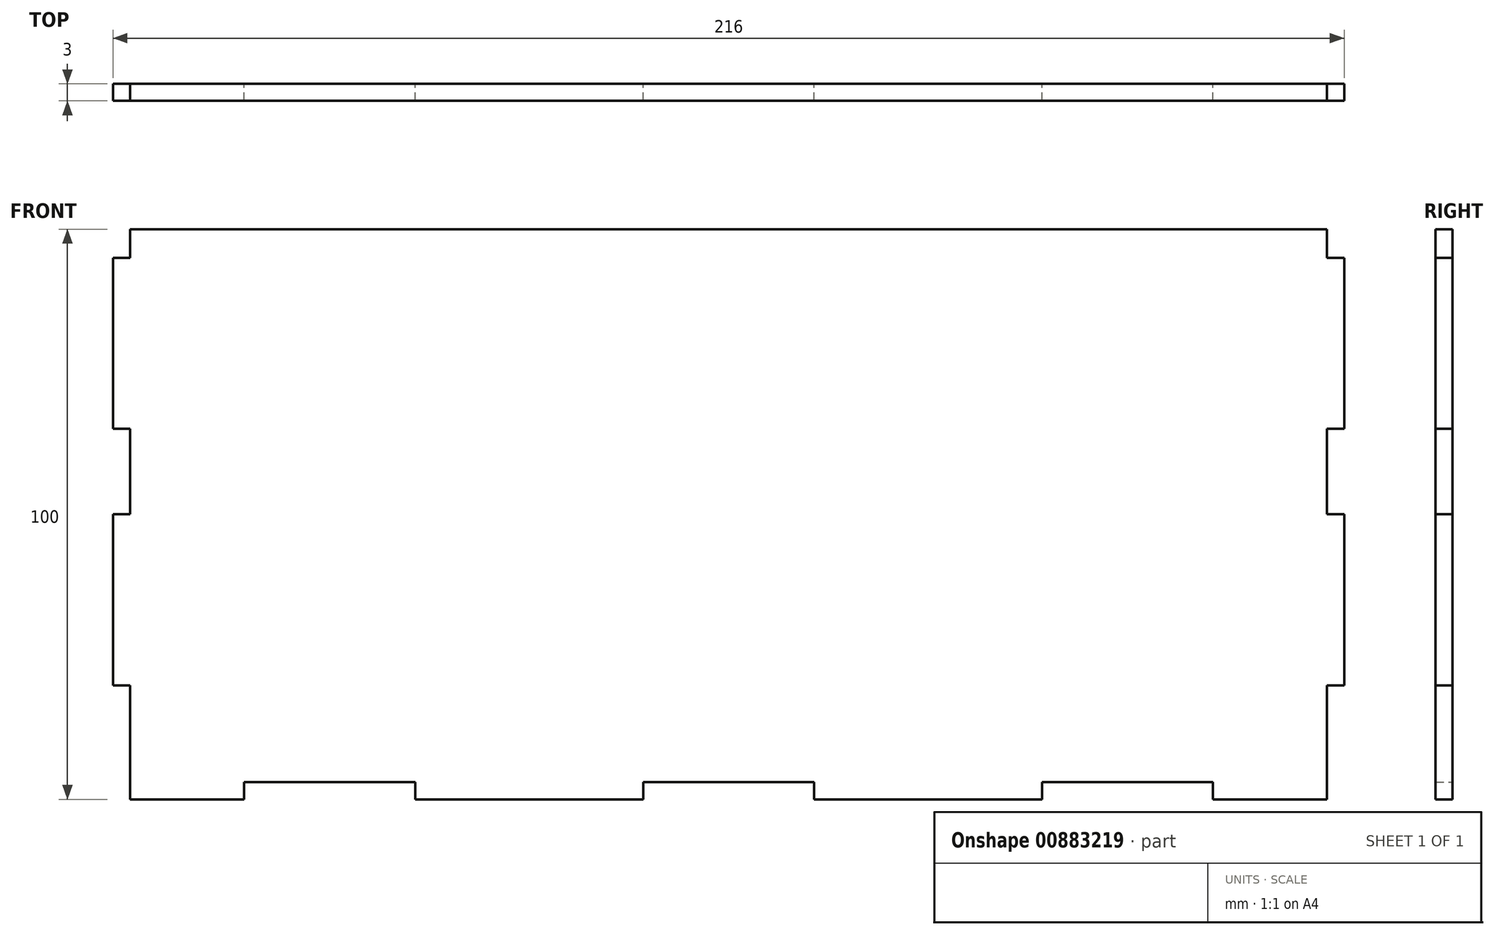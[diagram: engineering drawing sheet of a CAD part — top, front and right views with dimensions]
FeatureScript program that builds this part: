
annotation { "Feature Type Name" : "Feature", "Feature Type Description" : "" }
export const myFeature = defineFeature(function(context is Context, id is Id, definition is map)
    precondition{}
    {
        {
            var Q0;
            Q0=qCreatedBy(makeId("Front.planeOp"),FACE);
            var sketch = newSketch(context, id + "F0", { "sketchPlane" : qUnion([Q0])});
            skLineSegment(sketch, "E0.bottom", {"start": v(105, 50) * mm, "end": v(-105, 50) * mm});
            skLineSegment(sketch, "E0.top", {"start": v(105, -50) * mm, "end": v(-105, -50) * mm});
            skLineSegment(sketch, "E0.left", {"start": v(105, 50) * mm, "end": v(105, -50) * mm});
            skLineSegment(sketch, "E0.right", {"start": v(-105, 50) * mm, "end": v(-105, -50) * mm});
            skPoint(sketch, "E0.middle", {"position": v(0, 0) * mm});
            skLineSegment(sketch, "E1", {"start": v(55, -50) * mm, "end": v(55, -47) * mm});
            skLineSegment(sketch, "E2", {"start": v(55, -47) * mm, "end": v(85, -47) * mm});
            skLineSegment(sketch, "E3", {"start": v(85, -47) * mm, "end": v(85, -50) * mm});
            skLineSegment(sketch, "E4", {"start": v(105, -30) * mm, "end": v(108, -30) * mm});
            skLineSegment(sketch, "E5", {"start": v(108, -30) * mm, "end": v(108, 0) * mm});
            skLineSegment(sketch, "E6", {"start": v(108, 0) * mm, "end": v(105, 0) * mm});
            skLineSegment(sketch, "E7.MirrorCS", {"start": v(-105, -30) * mm, "end": v(-108, -30) * mm});
            skLineSegment(sketch, "E8.MirrorCS", {"start": v(-108, -30) * mm, "end": v(-108, 0) * mm});
            skLineSegment(sketch, "E9.MirrorCS", {"start": v(-108, 0) * mm, "end": v(-105, 0) * mm});
            skLineSegment(sketch, "E10", {"start": v(105, 45) * mm, "end": v(108, 45) * mm});
            skLineSegment(sketch, "E11", {"start": v(108, 45) * mm, "end": v(108, 15) * mm});
            skLineSegment(sketch, "E12", {"start": v(108, 15) * mm, "end": v(105, 15) * mm});
            skLineSegment(sketch, "E13.MirrorCS", {"start": v(-108, 15) * mm, "end": v(-105, 15) * mm});
            skLineSegment(sketch, "E14.MirrorCS", {"start": v(-108, 45) * mm, "end": v(-108, 15) * mm});
            skLineSegment(sketch, "E15.MirrorCS", {"start": v(-105, 45) * mm, "end": v(-108, 45) * mm});
            skLineSegment(sketch, "E16", {"start": v(-85, -50) * mm, "end": v(-85, -47) * mm});
            skLineSegment(sketch, "E17", {"start": v(-85, -47) * mm, "end": v(-55, -47) * mm});
            skLineSegment(sketch, "E18", {"start": v(-55, -47) * mm, "end": v(-55, -50) * mm});
            skLineSegment(sketch, "E19", {"start": v(-15, -50) * mm, "end": v(-15, -47) * mm});
            skLineSegment(sketch, "E20", {"start": v(-15, -47) * mm, "end": v(15, -47) * mm});
            skLineSegment(sketch, "E21", {"start": v(15, -47) * mm, "end": v(15, -50) * mm});
            skPoint(sketch, "E22", {"position": v(0, -47) * mm});
            skSolve(sketch);
        }
        {
            var Q0;
            Q0=makeQuery(id+"F0.imprint","IMPRINT",FACE,{"disambiguationData":[TD([[makeQuery(id+"F0.imprint","IMPRINT",EDGE,{"derivedFrom":sQuery(id+"F0.wireOp",EDGE,"E0.bottom")}),1.0]])]});
            var Q1;
            {var subQ0=sQuery(id+"F0.wireOp",EDGE,"E7.MirrorCS");Q1=makeQuery(id+"F0.imprint","IMPRINT",FACE,{"disambiguationData":[TD([[makeQuery(id+"F0.imprint","IMPRINT",EDGE,{"derivedFrom":subQ0}),-1.0]])]});}
            var Q2;
            {var subQ0=sQuery(id+"F0.wireOp",EDGE,"E4");Q2=makeQuery(id+"F0.imprint","IMPRINT",FACE,{"disambiguationData":[TD([[makeQuery(id+"F0.imprint","IMPRINT",EDGE,{"derivedFrom":subQ0}),1.0]])]});}
            var Q3;
            {var subQ0=sQuery(id+"F0.wireOp",EDGE,"E10");Q3=makeQuery(id+"F0.imprint","IMPRINT",FACE,{"disambiguationData":[TD([[makeQuery(id+"F0.imprint","IMPRINT",EDGE,{"derivedFrom":subQ0}),-1.0]])]});}
            var Q4;
            {var subQ0=sQuery(id+"F0.wireOp",EDGE,"E13.MirrorCS");Q4=makeQuery(id+"F0.imprint","IMPRINT",FACE,{"disambiguationData":[TD([[makeQuery(id+"F0.imprint","IMPRINT",EDGE,{"derivedFrom":subQ0}),1.0]])]});}
            extrude(context, id + "F1", {"entities" : qUnion([Q0, Q1, Q2, Q3, Q4]), "depth" : 3 * mm, "offsetDistance" : 25 * mm});
        }
    });
